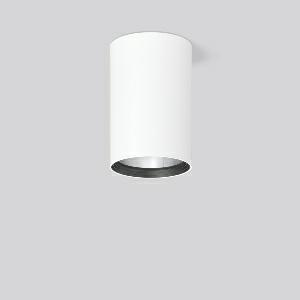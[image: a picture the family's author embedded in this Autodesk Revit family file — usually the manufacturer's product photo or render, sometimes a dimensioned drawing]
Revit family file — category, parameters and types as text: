
# Revit family: heledon_maxi_a_931219_002_76_3c77
name_source: partatom
category: Lighting Fixtures
units: mm (PartAtom-declared; Revit-internal decimal feet)

## family parameters
Cut with Voids When Loaded = No
Host = Face
Light Source = No
Part Type = Normal
Room Calculation Point = No
Round Connector Dimension = Use Diameter
Shared = No

## types (1)
- HELEDON maxi A (1 x LED Modul 930, 3250 lm, 3000)
    Apparent Load = 25 VA
    Approval mark = CE
    CIE Flux Codes = 97 100 100 100 100
    Color Rendering = 90
    Color Temperature = 3000
    Default Elevation = 1800 mm
    Description = Series: HELEDON maxi
Cylindrical surface-mounted downlight. Housing: die-cast aluminium, powder-coated. Internal ceiling frame polycarbonate with bayonet mounting. Black plastic ring and recessed LED to prevent glare from the side. Optical assembly with reflector made of MIRO-Silver with 98% total light reflection for outstanding efficiency - can be changed without tools. Best colour rendering index Ra>90. Suitable for Ceiling mounting. Easy installation with a separate ceiling frame with bayonet mounting and plug connection. Driver integrated. Connected via plug-in connector. High quality converter without flickering and stroboscopic effect. The following accessories can be mounted without use of tools: interchangeable lenses, decorative glasses, honeycomb louvre, clear and frosted diffusers, white interchangeable plastic ring. 
Colour: traffic white, matt (RAL 9016)
Diameter: 123 mm
Height: 183 mm
Lamp: LED
Socket: without socket
Colour temperature: 3000K
Colour rendering index (CRI): 92
System power: 25 W
Rated luminous flux: 3250 lm
Luminous efficiency: 130 lm/W
Control gear: Converter, dimmable, DALI
Protection class: I
Type of protection: IP 20
    Height = 183 mm
    Lamp = 1 x LED Modul 930
    Lamp Light Flux = 3250 lm
    Lamp count = 1
    Length = 123 mm
    Lifetime = 50000 h
    Luminous efficacy = 130 lm/W
    Manufacturer = RZB
    ModVariant = No
    Model = 931219.002.76
    Mounting Place = Ceiling
    Mounting Type = Surface mounted
    Number of Poles = 1
    OnlyDefault = Yes
    Power Factor = 1
    Product Name = HELEDON maxi A
    Product group = Surface mounted downlights
    ProductGroupID = 302
    Protection Class = Protection class I
    Protection Degree = IP 20
    RLX_Detail_Level = 1
    RLX_Emergency_Light_Flux = 0 lm
    RLX_Emergency_Type = 0
    RLX_Emergency_Type_DB = No
    RlxData = <blob elided: 97605 chars, md5=724174eb>
    Socket = socket
    Standby Power = 0 W
    System Light Flux = 3250 lm
    System Power = 25 W
    Type Comments = Product without accessories
    Type Image = 931192.002.jpg
    URL = http://relux.com
    VarID = ---
    Voltage = 230 V
    Voltage Range = 220-240 V
    Weight = 0.00 kg
    Width = 0 mm  [stored 0 ft]

note: [stored X ft] marks values corroborated as IEEE doubles in the binary element streams (Revit-internal decimal feet)

## geometry (parser evidence)
native form markers: Blend x4, Sweep x10
no freeform markers — native parametric forms only
